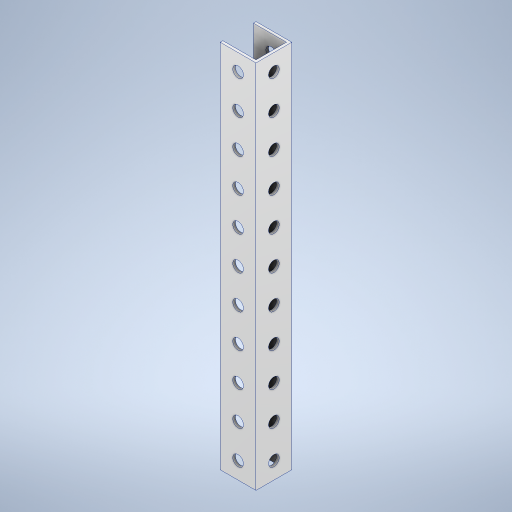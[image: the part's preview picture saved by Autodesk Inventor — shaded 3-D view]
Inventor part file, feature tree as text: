
AUTODESK INVENTOR PART (.ipt)
format: ipt  version: 2024 (Build 280153020, 153B)  size: 296,448 bytes
history: native  units: in
note: dims shown in document units (in); Inventor stores cm internally (conversion verified against a paired STEP export)
features: extrude x3, sketch x3, pattern_linear x1
ambient origin geometry x8: Origin, YZ Plane, XZ Plane, XY Plane, X Axis, Y Axis, Z Axis, Center Point
bodies: Solid1 (feature_tree)
feature tree (7):
  extrude  "Extrusion1"  Depth=1.063in
  sketch  "Sketch2"  dims[d2=0.0787in d3=11.0in d4=0.0in]
  sketch  "Sketch3"  dims[d5=0.5in d6=0.315in d7=0.5in d8=0.315in d9=3.6688in d10=0.0in d11=4.6437in d12=0.0in d13=4.3307in d15=1.0in]
  extrude  "Extrusion2"  Depth=11.0in TaperAngle=0.0deg
  extrude  "Extrusion3"  Depth=0.315in
  pattern_linear  "Rectangular Pattern1"  Spacing1=0.5in  [1 undecoded]
  sketch  "Sketch1"  dims[d0=1.063in d1=1.063in]
note: 1 required parameter value undecoded (feature->parameter linkage not recoverable at this tier; creation-order binding heuristic only, values carry confidence <= 0.55)
